# Revit family: EOS2.0m-WMM-I
name_source: partatom
category: Lighting Fixtures
revit_build: Autodesk Revit 2018 (Build: 20170223_1515(x64)
units: mm (PartAtom-declared; Revit-internal decimal feet)

## family parameters
Cut with Voids When Loaded = No
Host = Face
Light Source = Yes
Part Type = Normal
Room Calculation Point = Yes
Round Connector Dimension = Use Diameter
Shared = Yes

## types (6) — shared parameters
Color Filter = 16777215
Default Elevation = 7' - 0"
Dimming Lamp Color Temperature Shift = <None>
Emit Shape Visible in Rendering = Yes
Emit from Rectangle Width = 0' - 2"
Fixture Symbol Visiblity = Yes
Fixture Width = 0' - 2 1/4"
Lamp = LED
Light Source Symbol Size = 2' - 0"
Switch Leg Visibility = No
Voltage = 0 V

## per-type parameters (varying)
| type | Apparent Load | Emit from Rectangle Length | Fixture Length |
| 3' Indirect | 14 VA | 3' - 0" | 3' - 0" |
| 4' Indirect | 14 VA | 4' - 0" | 4' - 0" |
| 5' Indirect | 17 VA | 5' - 0" | 5' - 0" |
| 6' Indirect | 21 VA | 6' - 0" | 6' - 0" |
| 7' Indirect | 24 VA | 7' - 0" | 7' - 0" |
| 8' Indirect | 27 VA | 8' - 0" | 8' - 0" |

## geometry (parser evidence)
native form markers: Sweep x3
no freeform markers — native parametric forms only
